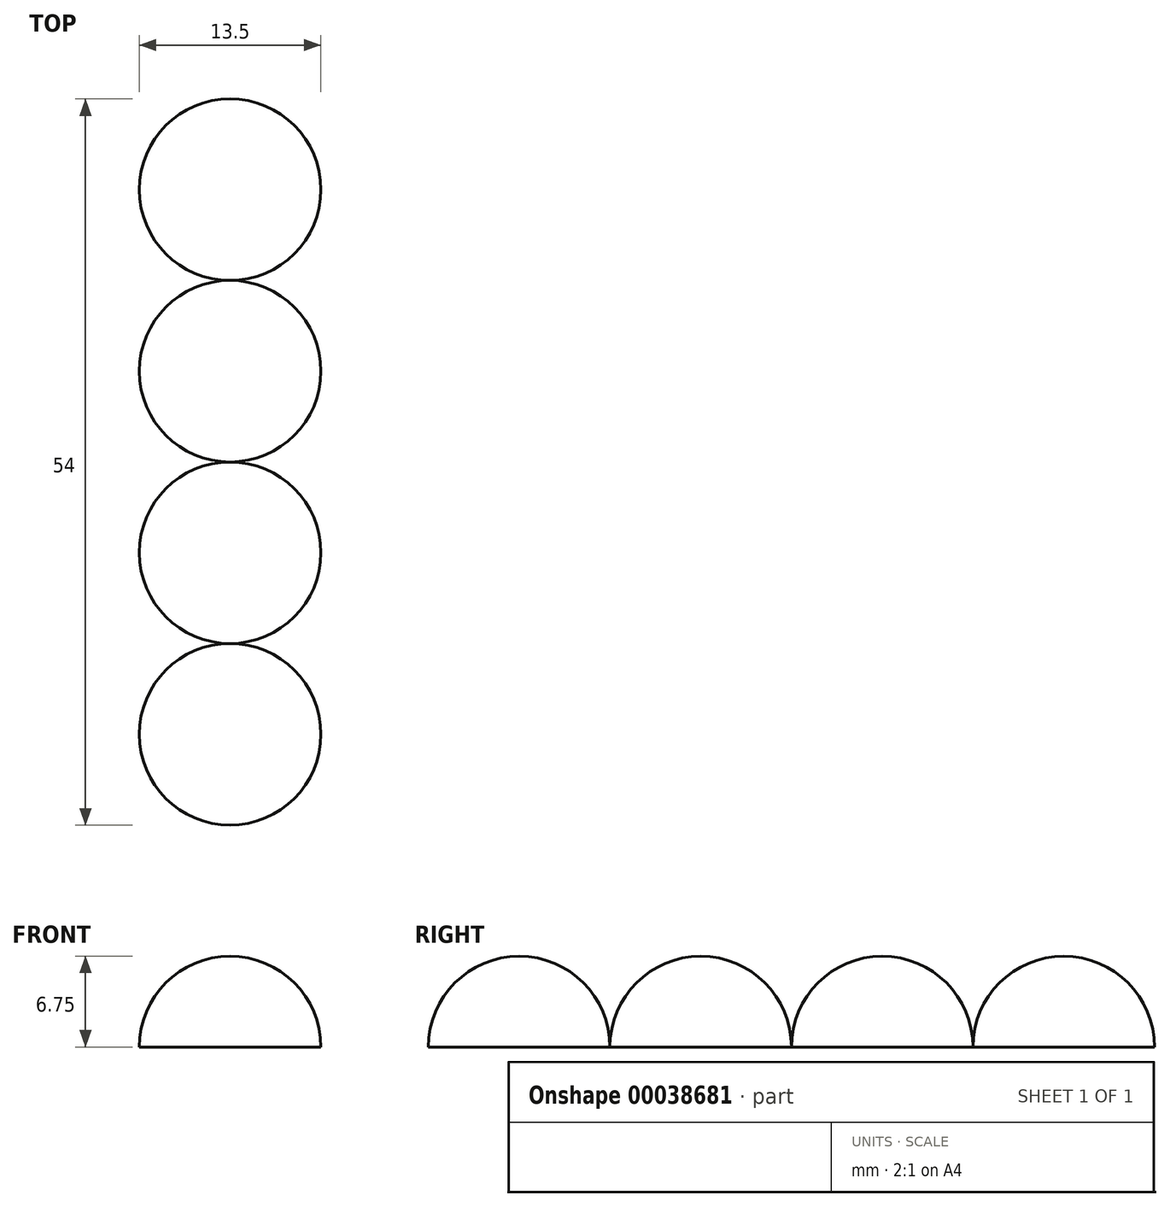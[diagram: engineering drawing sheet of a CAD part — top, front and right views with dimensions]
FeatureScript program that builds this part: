
annotation { "Feature Type Name" : "Feature", "Feature Type Description" : "" }
export const myFeature = defineFeature(function(context is Context, id is Id, definition is map)
    precondition{}
    {
        {
            var Q0;
            Q0=qCreatedBy(makeId("Top.planeOp"),FACE);
            var sketch = newSketch(context, id + "F0", { "sketchPlane" : qUnion([Q0])});
            skLineSegment(sketch, "E0", {"start": v(0, 0) * mm, "end": v(0, 13.5) * mm});
            skArc(sketch, "E1", {"start": v(0, 0) * mm, "mid": v(6.75, 6.75) * mm, "end": v(0, 13.5) * mm});
            skLineSegment(sketch, "E2", {"start": v(0, 0) * mm, "end": v(0, -13.5) * mm});
            skArc(sketch, "E3", {"start": v(0, -13.5) * mm, "mid": v(6.75, -6.75) * mm, "end": v(0, 0) * mm});
            skLineSegment(sketch, "E4", {"start": v(0, 13.5) * mm, "end": v(0, 27) * mm});
            skLineSegment(sketch, "E5", {"start": v(0, -13.5) * mm, "end": v(0, -27) * mm});
            skArc(sketch, "E6", {"start": v(0, 13.5) * mm, "mid": v(6.75, 20.25) * mm, "end": v(0, 27) * mm});
            skArc(sketch, "E7", {"start": v(0, -27) * mm, "mid": v(6.75, -20.25) * mm, "end": v(0, -13.5) * mm});
            skSolve(sketch);
        }
        {
            var Q0;
            Q0=qSketchRegion(id+"F0",true);
            var Q1;
            Q1=sQuery(id+"F0.wireOp",EDGE,"E0");
            revolve(context, id + "F1", {"entities" : qUnion([Q0]), "axis" : qUnion([Q1]), "revolveType" : RevolveType.ONE_DIRECTION, "oppositeDirection" : true, "angle" : 180 * degree});
        }
    });
